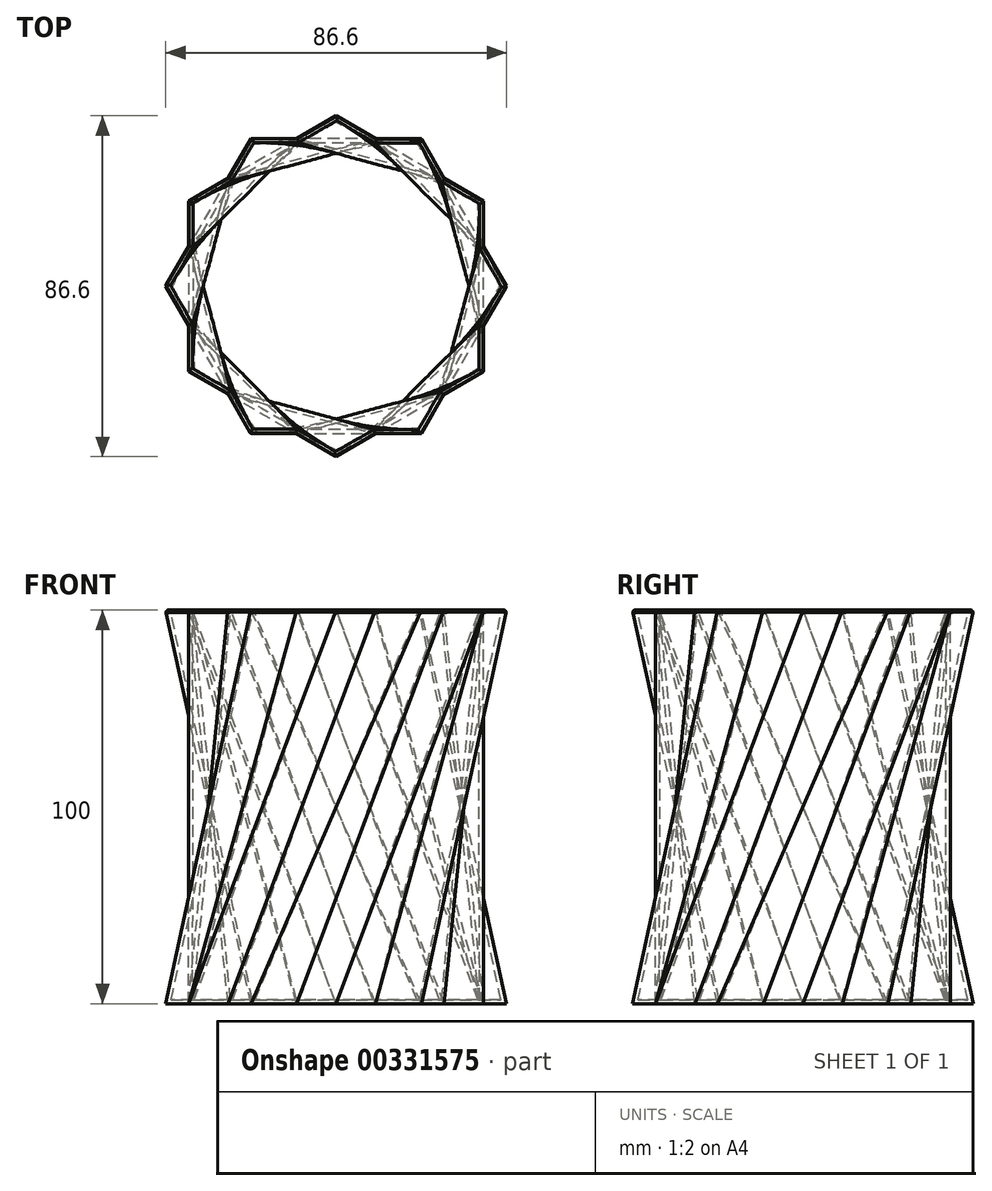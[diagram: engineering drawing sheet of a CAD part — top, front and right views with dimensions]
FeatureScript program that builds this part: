
annotation { "Feature Type Name" : "Feature", "Feature Type Description" : "" }
export const myFeature = defineFeature(function(context is Context, id is Id, definition is map)
    precondition{}
    {
        {
            var Q0;
            Q0=qCreatedBy(makeId("Top.planeOp"),FACE);
            var sketch = newSketch(context, id + "F0", { "sketchPlane" : qUnion([Q0])});
            skCircle(sketch, "E0.cCircle", {"center": v(0, 0) * mm, "radius": 37.5 * mm, "construction": true});
            skLineSegment(sketch, "E0.0", {"start": v(-21.65, 37.5) * mm, "end": v(-10.05, 37.5) * mm});
            skLineSegment(sketch, "E0.1", {"start": v(21.65, 37.5) * mm, "end": v(27.45, 27.45) * mm});
            skLineSegment(sketch, "E0.2", {"start": v(43.3, 0) * mm, "end": v(37.5, -10.05) * mm});
            skLineSegment(sketch, "E0.3", {"start": v(21.65, -37.5) * mm, "end": v(10.05, -37.5) * mm});
            skLineSegment(sketch, "E0.4", {"start": v(-21.65, -37.5) * mm, "end": v(-27.45, -27.45) * mm});
            skLineSegment(sketch, "E0.5", {"start": v(-43.3, 0) * mm, "end": v(-37.5, 10.05) * mm});
            skPoint(sketch, "E0.0.midPoint", {"position": v(0, 37.5) * mm});
            skLineSegment(sketch, "E1.0", {"start": v(-37.5, -21.65) * mm, "end": v(-37.5, -10.05) * mm});
            skLineSegment(sketch, "E1.1", {"start": v(-37.5, 21.65) * mm, "end": v(-27.45, 27.45) * mm});
            skLineSegment(sketch, "E1.2", {"start": v(0, 43.3) * mm, "end": v(10.05, 37.5) * mm});
            skLineSegment(sketch, "E1.3", {"start": v(37.5, 21.65) * mm, "end": v(37.5, 10.05) * mm});
            skLineSegment(sketch, "E1.4", {"start": v(37.5, -21.65) * mm, "end": v(27.45, -27.45) * mm});
            skLineSegment(sketch, "E1.5", {"start": v(0, -43.3) * mm, "end": v(-10.05, -37.5) * mm});
            skPoint(sketch, "E1.0.midPoint", {"position": v(-37.5, 0) * mm});
            skLineSegment(sketch, "E2.trimOffspring", {"start": v(-10.05, 37.5) * mm, "end": v(0, 43.3) * mm});
            skLineSegment(sketch, "E3.trimOffspring", {"start": v(-27.45, 27.45) * mm, "end": v(-21.65, 37.5) * mm});
            skLineSegment(sketch, "E4.trimOffspring", {"start": v(-37.5, 10.05) * mm, "end": v(-37.5, 21.65) * mm});
            skLineSegment(sketch, "E5.trimOffspring", {"start": v(-37.5, -10.05) * mm, "end": v(-43.3, 0) * mm});
            skLineSegment(sketch, "E6.trimOffspring", {"start": v(-27.45, -27.45) * mm, "end": v(-37.5, -21.65) * mm});
            skLineSegment(sketch, "E7.trimOffspring", {"start": v(-10.05, -37.5) * mm, "end": v(-21.65, -37.5) * mm});
            skLineSegment(sketch, "E8.trimOffspring", {"start": v(10.05, -37.5) * mm, "end": v(0, -43.3) * mm});
            skLineSegment(sketch, "E9.trimOffspring", {"start": v(27.45, -27.45) * mm, "end": v(21.65, -37.5) * mm});
            skLineSegment(sketch, "E10.trimOffspring", {"start": v(37.5, -10.05) * mm, "end": v(37.5, -21.65) * mm});
            skLineSegment(sketch, "E11.trimOffspring", {"start": v(37.5, 10.05) * mm, "end": v(43.3, 0) * mm});
            skLineSegment(sketch, "E12.trimOffspring", {"start": v(27.45, 27.45) * mm, "end": v(37.5, 21.65) * mm});
            skLineSegment(sketch, "E13.trimOffspring", {"start": v(10.05, 37.5) * mm, "end": v(21.65, 37.5) * mm});
            skSolve(sketch);
        }
        {
            var Q0;
            Q0=qCreatedBy(makeId("Top.planeOp"),FACE);
            cPlane(context, id + "F1", {"entities" : qUnion([Q0]), "cplaneType" : CPlaneType.OFFSET, "offset" : 100 * mm, "width" : 150 * mm, "height" : 150 * mm});
        }
        {
            var Q0;
            Q0=qCreatedBy(id+"F1.planeOp",FACE);
            var sketch = newSketch(context, id + "F2", { "sketchPlane" : qUnion([Q0])});
            skLineSegment(sketch, "E14.0", {"start": v(43.3, 0) * mm, "end": v(37.5, -10.05) * mm});
            skLineSegment(sketch, "E14.1", {"start": v(21.65, 37.5) * mm, "end": v(27.45, 27.45) * mm});
            skLineSegment(sketch, "E14.2", {"start": v(-21.65, 37.5) * mm, "end": v(-10.05, 37.5) * mm});
            skLineSegment(sketch, "E14.3", {"start": v(-27.45, 27.45) * mm, "end": v(-21.65, 37.5) * mm});
            skLineSegment(sketch, "E14.4", {"start": v(-21.65, -37.5) * mm, "end": v(-27.45, -27.45) * mm});
            skLineSegment(sketch, "E14.5", {"start": v(-43.3, 0) * mm, "end": v(-37.5, 10.05) * mm});
            skLineSegment(sketch, "E14.7", {"start": v(-37.5, -21.65) * mm, "end": v(-37.5, -10.05) * mm});
            skLineSegment(sketch, "E14.8", {"start": v(-37.5, 10.05) * mm, "end": v(-37.5, 21.65) * mm});
            skLineSegment(sketch, "E14.9", {"start": v(-37.5, 21.65) * mm, "end": v(-27.45, 27.45) * mm});
            skLineSegment(sketch, "E14.10", {"start": v(0, 43.3) * mm, "end": v(10.05, 37.5) * mm});
            skLineSegment(sketch, "E14.11", {"start": v(37.5, 21.65) * mm, "end": v(37.5, 10.05) * mm});
            skLineSegment(sketch, "E14.12", {"start": v(-27.45, -27.45) * mm, "end": v(-37.5, -21.65) * mm});
            skLineSegment(sketch, "E14.13", {"start": v(10.05, 37.5) * mm, "end": v(21.65, 37.5) * mm});
            skLineSegment(sketch, "E14.14", {"start": v(37.5, -21.65) * mm, "end": v(27.45, -27.45) * mm});
            skLineSegment(sketch, "E14.15", {"start": v(37.5, 10.05) * mm, "end": v(43.3, 0) * mm});
            skLineSegment(sketch, "E14.16", {"start": v(37.5, -10.05) * mm, "end": v(37.5, -21.65) * mm});
            skLineSegment(sketch, "E14.17", {"start": v(-10.05, 37.5) * mm, "end": v(0, 43.3) * mm});
            skLineSegment(sketch, "E14.18", {"start": v(-37.5, -10.05) * mm, "end": v(-43.3, 0) * mm});
            skLineSegment(sketch, "E14.19", {"start": v(27.45, -27.45) * mm, "end": v(21.65, -37.5) * mm});
            skLineSegment(sketch, "E14.20", {"start": v(27.45, 27.45) * mm, "end": v(37.5, 21.65) * mm});
            skLineSegment(sketch, "E15.0", {"start": v(21.65, -37.5) * mm, "end": v(10.05, -37.5) * mm});
            skLineSegment(sketch, "E15.1", {"start": v(10.05, -37.5) * mm, "end": v(0, -43.3) * mm});
            skLineSegment(sketch, "E15.2", {"start": v(0, -43.3) * mm, "end": v(-10.05, -37.5) * mm});
            skLineSegment(sketch, "E15.3", {"start": v(-10.05, -37.5) * mm, "end": v(-21.65, -37.5) * mm});
            skSolve(sketch);
        }
        {
            var Q0;
            Q0=makeQuery(id+"F0.imprint","IMPRINT",FACE,{"disambiguationData":[TD([[makeQuery(id+"F0.imprint","IMPRINT",EDGE,{"derivedFrom":sQuery(id+"F0.wireOp",EDGE,"E0.0")}),-1.0]])]});
            var Q1;
            Q1=makeQuery(id+"F2.imprint","IMPRINT",FACE,{"disambiguationData":[TD([[makeQuery(id+"F2.imprint","IMPRINT",EDGE,{"derivedFrom":sQuery(id+"F2.wireOp",EDGE,"E14.0")}),-1.0]])]});
            var Q2;
            Q2=sQuery(id+"F2.wireOp",VERTEX,"E14.18.end");
            var Q3;
            Q3=sQuery(id+"F0.wireOp",VERTEX,"E3.trimOffspring.end");
            loft(context, id + "F3", {"sheetProfilesArray" : [{ "sheetProfileEntities" : qUnion([Q0]) }, { "sheetProfileEntities" : qUnion([Q1]) }], "matchConnections" : true, "connections" : [{ "connectionEntities" : qUnion([Q2, Q3]), "connectionEdgeQueries" : qUnion([]), "connectionEdgeParameters" : [] }]});
        }
        {
            var Q0;
            Q0=makeQuery(id+"F3.opLoft","CAP_FACE",FACE,{"disambiguationData":[OSD([makeQuery(id+"F2.imprint","IMPRINT",FACE,{"disambiguationData":[TD([[makeQuery(id+"F2.imprint","IMPRINT",EDGE,{"derivedFrom":sQuery(id+"F2.wireOp",EDGE,"E14.0")}),-1.0]])]})])],"isStart":true});
            shell(context, id + "F4", {"entities" : qUnion([Q0]), "thickness" : 1 * mm});
        }
        {
            var Q0;
            Q0=makeQuery(id+"F3.opLoft","CAP_FACE",FACE,{"disambiguationData":[OSD([makeQuery(id+"F2.imprint","IMPRINT",FACE,{"disambiguationData":[TD([[makeQuery(id+"F2.imprint","IMPRINT",EDGE,{"derivedFrom":sQuery(id+"F2.wireOp",EDGE,"E14.0")}),-1.0]])]})])],"isStart":true});
            fillet(context, id + "F5", {"entities" : qUnion([Q0]), "radius" : 0.5 * mm, "tangentPropagation" : true, "allowEdgeOverflow" : false});
        }
    });
